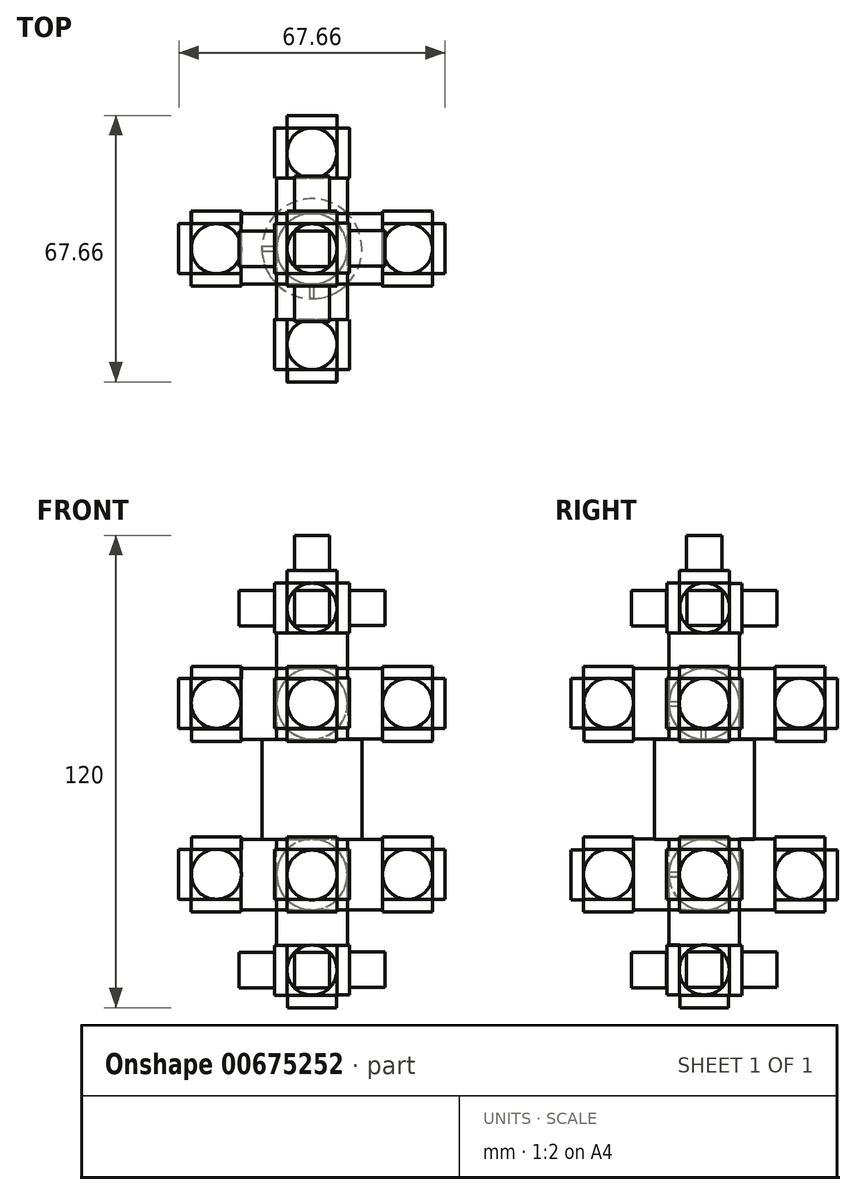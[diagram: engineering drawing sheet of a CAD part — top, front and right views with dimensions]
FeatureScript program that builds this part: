
annotation { "Feature Type Name" : "Feature", "Feature Type Description" : "" }
export const myFeature = defineFeature(function(context is Context, id is Id, definition is map)
    precondition{}
    {
        {
            var Q0;
            Q0=qCreatedBy(makeId("Top.planeOp"),FACE);
            var sketch = newSketch(context, id + "F0", { "sketchPlane" : qUnion([Q0])});
            skCircle(sketch, "E0", {"center": v(0, 0) * mm, "radius": 12.7 * mm});
            skSolve(sketch);
        }
        {
            var Q0;
            Q0=makeQuery(id+"F0.imprint","IMPRINT",FACE,{"disambiguationData":[TD([[makeQuery(id+"F0.imprint","IMPRINT",EDGE,{"derivedFrom":sQuery(id+"F0.wireOp",EDGE,"E0")}),1.0]])]});
            extrude(context, id + "F1", {"entities" : qUnion([Q0]), "depth" : 25.4 * mm, "offsetDistance" : 25.4 * mm});
        }
        {
            var Q0;
            Q0=qCreatedBy(makeId("Top.planeOp"),FACE);
            cPlane(context, id + "F2", {"entities" : qUnion([Q0]), "cplaneType" : CPlaneType.OFFSET, "offset" : 25.4 * mm, "width" : 152.4 * mm, "height" : 152.4 * mm});
        }
        {
            var Q0;
            Q0=qCreatedBy(id+"F2.planeOp",FACE);
            var sketch = newSketch(context, id + "F3", { "sketchPlane" : qUnion([Q0])});
            skLineSegment(sketch, "E1.bottom", {"start": v(-8.98, 8.98) * mm, "end": v(8.98, 8.98) * mm});
            skLineSegment(sketch, "E1.top", {"start": v(-8.98, -8.98) * mm, "end": v(8.98, -8.98) * mm});
            skLineSegment(sketch, "E1.left", {"start": v(-8.98, 8.98) * mm, "end": v(-8.98, -8.98) * mm});
            skLineSegment(sketch, "E1.right", {"start": v(8.98, 8.98) * mm, "end": v(8.98, -8.98) * mm});
            skPoint(sketch, "E1.middle", {"position": v(0, 0) * mm});
            skSolve(sketch);
        }
        {
            var Q0;
            Q0=makeQuery(id+"F3.imprint","IMPRINT",FACE,{"disambiguationData":[TD([[makeQuery(id+"F3.imprint","IMPRINT",EDGE,{"derivedFrom":sQuery(id+"F3.wireOp",EDGE,"E1.bottom")}),-1.0]])]});
            extrude(context, id + "F4", {"entities" : qUnion([Q0]), "operationType" : NewBodyOperationType.ADD, "depth" : 17.96 * mm, "offsetDistance" : 25.4 * mm});
        }
        {
            var Q0;
            Q0=qCreatedBy(makeId("Top.planeOp"),FACE);
            var sketch = newSketch(context, id + "F5", { "sketchPlane" : qUnion([Q0])});
            skLineSegment(sketch, "E2.bottom", {"start": v(-8.98, -8.98) * mm, "end": v(8.98, -8.98) * mm});
            skLineSegment(sketch, "E2.top", {"start": v(-8.98, 8.98) * mm, "end": v(8.98, 8.98) * mm});
            skLineSegment(sketch, "E2.left", {"start": v(-8.98, -8.98) * mm, "end": v(-8.98, 8.98) * mm});
            skLineSegment(sketch, "E2.right", {"start": v(8.98, -8.98) * mm, "end": v(8.98, 8.98) * mm});
            skPoint(sketch, "E2.middle", {"position": v(0, 0) * mm});
            skSolve(sketch);
        }
        {
            var Q0;
            Q0=makeQuery(id+"F5.imprint","IMPRINT",FACE,{"disambiguationData":[TD([[makeQuery(id+"F5.imprint","IMPRINT",EDGE,{"derivedFrom":sQuery(id+"F5.wireOp",EDGE,"E2.bottom")}),1.0]])]});
            extrude(context, id + "F6", {"entities" : qUnion([Q0]), "operationType" : NewBodyOperationType.ADD, "oppositeDirection" : true, "depth" : 17.96 * mm, "offsetDistance" : 25.4 * mm});
        }
        {
            var Q0;
            Q0=qCreatedBy(makeId("Right.planeOp"),FACE);
            cPlane(context, id + "F7", {"entities" : qUnion([Q0]), "cplaneType" : CPlaneType.OFFSET, "offset" : 8.98 * mm, "width" : 152.4 * mm, "height" : 152.4 * mm});
        }
        {
            var Q0;
            Q0=qCreatedBy(makeId("Right.planeOp"),FACE);
            cPlane(context, id + "F8", {"entities" : qUnion([Q0]), "cplaneType" : CPlaneType.OFFSET, "offset" : 8.98 * mm, "oppositeDirection" : true, "width" : 152.4 * mm, "height" : 152.4 * mm});
        }
        {
            var Q0;
            Q0=qCreatedBy(id+"F8.planeOp",FACE);
            var sketch = newSketch(context, id + "F9", { "sketchPlane" : qUnion([Q0])});
            skCircle(sketch, "E3", {"center": v(0, 34.36) * mm, "radius": 8.98 * mm});
            skSolve(sketch);
        }
        {
            var Q0;
            Q0=makeQuery(id+"F9.imprint","IMPRINT",FACE,{"disambiguationData":[TD([[makeQuery(id+"F9.imprint","IMPRINT",EDGE,{"derivedFrom":sQuery(id+"F9.wireOp",EDGE,"E3")}),1.0]])]});
            extrude(context, id + "F10", {"entities" : qUnion([Q0]), "operationType" : NewBodyOperationType.ADD, "oppositeDirection" : true, "depth" : 8.98 * mm, "offsetDistance" : 25.4 * mm});
        }
        {
            var Q0;
            Q0=qCreatedBy(id+"F2.planeOp",FACE);
            cPlane(context, id + "F11", {"entities" : qUnion([Q0]), "cplaneType" : CPlaneType.OFFSET, "offset" : 17.96 * mm, "width" : 152.4 * mm, "height" : 152.4 * mm});
        }
        {
            var Q0;
            Q0=qCreatedBy(id+"F11.planeOp",FACE);
            var sketch = newSketch(context, id + "F12", { "sketchPlane" : qUnion([Q0])});
            skCircle(sketch, "E4", {"center": v(0, 0) * mm, "radius": 8.98 * mm});
            skSolve(sketch);
        }
        {
            var Q0;
            Q0=makeQuery(id+"F12.imprint","IMPRINT",FACE,{"disambiguationData":[TD([[makeQuery(id+"F12.imprint","IMPRINT",EDGE,{"derivedFrom":sQuery(id+"F12.wireOp",EDGE,"E4")}),1.0]])]});
            extrude(context, id + "F13", {"entities" : qUnion([Q0]), "operationType" : NewBodyOperationType.ADD, "depth" : 8.98 * mm, "offsetDistance" : 25.4 * mm});
        }
        {
            var Q0;
            Q0=qCreatedBy(id+"F8.planeOp",FACE);
            var sketch = newSketch(context, id + "F14", { "sketchPlane" : qUnion([Q0])});
            skCircle(sketch, "E5", {"center": v(0, -9.05) * mm, "radius": 8.98 * mm});
            skSolve(sketch);
        }
        {
            var Q0;
            Q0=makeQuery(id+"F14.imprint","IMPRINT",FACE,{"disambiguationData":[TD([[makeQuery(id+"F14.imprint","IMPRINT",EDGE,{"derivedFrom":sQuery(id+"F14.wireOp",EDGE,"E5")}),1.0]])]});
            var Q1;
            Q1=sQuery(id+"F14.wireOp",EDGE,"E5");
            extrude(context, id + "F15", {"entities" : qUnion([Q0]), "operationType" : NewBodyOperationType.ADD, "surfaceEntities" : qUnion([Q1]), "oppositeDirection" : true, "depth" : 8.98 * mm, "offsetDistance" : 25.4 * mm});
        }
        {
            var Q0;
            Q0=qCreatedBy(id+"F7.planeOp",FACE);
            var sketch = newSketch(context, id + "F16", { "sketchPlane" : qUnion([Q0])});
            skCircle(sketch, "E6", {"center": v(0, -9) * mm, "radius": 8.98 * mm});
            skSolve(sketch);
        }
        {
            var Q0;
            Q0=makeQuery(id+"F16.imprint","IMPRINT",FACE,{"disambiguationData":[TD([[makeQuery(id+"F16.imprint","IMPRINT",EDGE,{"derivedFrom":sQuery(id+"F16.wireOp",EDGE,"E6")}),1.0]])]});
            var Q1;
            Q1=sQuery(id+"F16.wireOp",EDGE,"E6");
            extrude(context, id + "F17", {"entities" : qUnion([Q0]), "operationType" : NewBodyOperationType.ADD, "surfaceEntities" : qUnion([Q1]), "depth" : 8.98 * mm, "offsetDistance" : 25.4 * mm});
        }
        {
            var Q0;
            Q0=qCreatedBy(id+"F7.planeOp",FACE);
            var sketch = newSketch(context, id + "F18", { "sketchPlane" : qUnion([Q0])});
            skCircle(sketch, "E7", {"center": v(0, 34.4) * mm, "radius": 8.98 * mm});
            skSolve(sketch);
        }
        {
            var Q0;
            Q0=makeQuery(id+"F18.imprint","IMPRINT",FACE,{"disambiguationData":[TD([[makeQuery(id+"F18.imprint","IMPRINT",EDGE,{"derivedFrom":sQuery(id+"F18.wireOp",EDGE,"E7")}),1.0]])]});
            var Q1;
            Q1=sQuery(id+"F18.wireOp",EDGE,"E7");
            extrude(context, id + "F19", {"entities" : qUnion([Q0]), "operationType" : NewBodyOperationType.ADD, "surfaceEntities" : qUnion([Q1]), "depth" : 8.98 * mm, "offsetDistance" : 25.4 * mm});
        }
        {
            var Q0;
            Q0=qCreatedBy(makeId("Front.planeOp"),FACE);
            cPlane(context, id + "F20", {"entities" : qUnion([Q0]), "cplaneType" : CPlaneType.OFFSET, "offset" : 8.98 * mm, "width" : 152.4 * mm, "height" : 152.4 * mm});
        }
        {
            var Q0;
            Q0=qCreatedBy(id+"F20.planeOp",FACE);
            var sketch = newSketch(context, id + "F21", { "sketchPlane" : qUnion([Q0])});
            skCircle(sketch, "E8", {"center": v(0, -8.96) * mm, "radius": 8.98 * mm});
            skSolve(sketch);
        }
        {
            var Q0;
            Q0=makeQuery(id+"F21.imprint","IMPRINT",FACE,{"disambiguationData":[TD([[makeQuery(id+"F21.imprint","IMPRINT",EDGE,{"derivedFrom":sQuery(id+"F21.wireOp",EDGE,"E8")}),1.0]])]});
            var Q1;
            Q1=sQuery(id+"F21.wireOp",EDGE,"E8");
            extrude(context, id + "F22", {"entities" : qUnion([Q0]), "operationType" : NewBodyOperationType.ADD, "surfaceEntities" : qUnion([Q1]), "depth" : 8.98 * mm, "offsetDistance" : 25.4 * mm});
        }
        {
            var Q0;
            Q0=qCreatedBy(id+"F20.planeOp",FACE);
            var sketch = newSketch(context, id + "F23", { "sketchPlane" : qUnion([Q0])});
            skCircle(sketch, "E9", {"center": v(0, 34.39) * mm, "radius": 8.98 * mm});
            skSolve(sketch);
        }
        {
            var Q0;
            Q0=makeQuery(id+"F23.imprint","IMPRINT",FACE,{"disambiguationData":[TD([[makeQuery(id+"F23.imprint","IMPRINT",EDGE,{"derivedFrom":sQuery(id+"F23.wireOp",EDGE,"E9")}),1.0]])]});
            var Q1;
            Q1=sQuery(id+"F23.wireOp",EDGE,"E9");
            extrude(context, id + "F24", {"entities" : qUnion([Q0]), "surfaceEntities" : qUnion([Q1]), "depth" : 8.98 * mm, "offsetDistance" : 25.4 * mm});
        }
        {
            var Q0;
            Q0=qCreatedBy(makeId("Front.planeOp"),FACE);
            cPlane(context, id + "F25", {"entities" : qUnion([Q0]), "cplaneType" : CPlaneType.OFFSET, "offset" : 8.98 * mm, "oppositeDirection" : true, "width" : 152.4 * mm, "height" : 152.4 * mm});
        }
        {
            var Q0;
            Q0=qCreatedBy(id+"F25.planeOp",FACE);
            var sketch = newSketch(context, id + "F26", { "sketchPlane" : qUnion([Q0])});
            skCircle(sketch, "E10", {"center": v(0, -8.98) * mm, "radius": 8.98 * mm});
            skCircle(sketch, "E11", {"center": v(0, 34.43) * mm, "radius": 8.97 * mm});
            skSolve(sketch);
        }
        {
            var Q0;
            Q0 = qSketchRegion(id + "F26", true);
            extrude(context, id + "F27", {"entities" : qUnion([Q0]), "oppositeDirection" : true, "depth" : 8.98 * mm, "offsetDistance" : 25.4 * mm});
        }
        {
            var Q0;
            Q0=qCreatedBy(makeId("Top.planeOp"),FACE);
            cPlane(context, id + "F28", {"entities" : qUnion([Q0]), "cplaneType" : CPlaneType.OFFSET, "offset" : 17.96 * mm, "oppositeDirection" : true, "width" : 152.4 * mm, "height" : 152.4 * mm});
        }
        {
            var Q0;
            Q0=qCreatedBy(id+"F28.planeOp",FACE);
            var sketch = newSketch(context, id + "F29", { "sketchPlane" : qUnion([Q0])});
            skCircle(sketch, "E12", {"center": v(0, 0) * mm, "radius": 8.98 * mm});
            skSolve(sketch);
        }
        {
            var Q0;
            Q0 = qSketchRegion(id + "F29", true);
            extrude(context, id + "F30", {"entities" : qUnion([Q0]), "oppositeDirection" : true, "depth" : 8.98 * mm, "offsetDistance" : 25.4 * mm});
        }
        {
            var Q0;
            Q0=qCreatedBy(id+"F28.planeOp",FACE);
            cPlane(context, id + "F31", {"entities" : qUnion([Q0]), "cplaneType" : CPlaneType.OFFSET, "offset" : 8.98 * mm, "oppositeDirection" : true, "width" : 152.4 * mm, "height" : 152.4 * mm});
        }
        {
            var Q0;
            Q0=qCreatedBy(id+"F31.planeOp",FACE);
            var sketch = newSketch(context, id + "F32", { "sketchPlane" : qUnion([Q0])});
            skLineSegment(sketch, "E13.bottom", {"start": v(-6.35, -6.35) * mm, "end": v(6.35, -6.35) * mm});
            skLineSegment(sketch, "E13.top", {"start": v(-6.35, 6.35) * mm, "end": v(6.35, 6.35) * mm});
            skLineSegment(sketch, "E13.left", {"start": v(-6.35, -6.35) * mm, "end": v(-6.35, 6.35) * mm});
            skLineSegment(sketch, "E13.right", {"start": v(6.35, -6.35) * mm, "end": v(6.35, 6.35) * mm});
            skPoint(sketch, "E13.middle", {"position": v(0, 0) * mm});
            skSolve(sketch);
        }
        {
            var Q0;
            Q0=makeQuery(id+"F32.imprint","IMPRINT",FACE,{"disambiguationData":[TD([[makeQuery(id+"F32.imprint","IMPRINT",EDGE,{"derivedFrom":sQuery(id+"F32.wireOp",EDGE,"E13.bottom")}),1.0]])]});
            extrude(context, id + "F33", {"entities" : qUnion([Q0]), "operationType" : NewBodyOperationType.ADD, "oppositeDirection" : true, "depth" : 12.7 * mm, "offsetDistance" : 25.4 * mm});
        }
        {
            var Q0;
            Q0=qCreatedBy(id+"F7.planeOp",FACE);
            cPlane(context, id + "F34", {"entities" : qUnion([Q0]), "cplaneType" : CPlaneType.OFFSET, "offset" : 8.98 * mm, "width" : 152.4 * mm, "height" : 152.4 * mm});
        }
        {
            var Q0;
            Q0=qCreatedBy(id+"F34.planeOp",FACE);
            var sketch = newSketch(context, id + "F35", { "sketchPlane" : qUnion([Q0])});
            skLineSegment(sketch, "E14.bottom", {"start": v(-6.35, 40.78) * mm, "end": v(6.35, 40.78) * mm});
            skLineSegment(sketch, "E14.top", {"start": v(-6.35, 28.08) * mm, "end": v(6.35, 28.08) * mm});
            skLineSegment(sketch, "E14.left", {"start": v(-6.35, 40.78) * mm, "end": v(-6.35, 28.08) * mm});
            skLineSegment(sketch, "E14.right", {"start": v(6.35, 40.78) * mm, "end": v(6.35, 28.08) * mm});
            skPoint(sketch, "E14.middle", {"position": v(0, 34.43) * mm});
            skLineSegment(sketch, "E15.bottom", {"start": v(-6.35, -2.63) * mm, "end": v(6.35, -2.63) * mm});
            skLineSegment(sketch, "E15.top", {"start": v(-6.35, -15.33) * mm, "end": v(6.35, -15.33) * mm});
            skLineSegment(sketch, "E15.left", {"start": v(-6.35, -2.63) * mm, "end": v(-6.35, -15.33) * mm});
            skLineSegment(sketch, "E15.right", {"start": v(6.35, -2.63) * mm, "end": v(6.35, -15.33) * mm});
            skPoint(sketch, "E15.middle", {"position": v(0, -8.98) * mm});
            skSolve(sketch);
        }
        {
            var Q0;
            Q0 = qSketchRegion(id + "F35", true);
            extrude(context, id + "F36", {"entities" : qUnion([Q0]), "operationType" : NewBodyOperationType.ADD, "depth" : 12.7 * mm, "offsetDistance" : 25.4 * mm});
        }
        {
            var Q0;
            Q0=qCreatedBy(id+"F8.planeOp",FACE);
            cPlane(context, id + "F37", {"entities" : qUnion([Q0]), "cplaneType" : CPlaneType.OFFSET, "offset" : 8.98 * mm, "oppositeDirection" : true, "width" : 152.4 * mm, "height" : 152.4 * mm});
        }
        {
            var Q0;
            Q0=qCreatedBy(id+"F37.planeOp",FACE);
            var sketch = newSketch(context, id + "F38", { "sketchPlane" : qUnion([Q0])});
            skLineSegment(sketch, "E16.bottom", {"start": v(6.35, -2.63) * mm, "end": v(-6.35, -2.63) * mm});
            skLineSegment(sketch, "E16.top", {"start": v(6.35, -15.33) * mm, "end": v(-6.35, -15.33) * mm});
            skLineSegment(sketch, "E16.left", {"start": v(6.35, -2.63) * mm, "end": v(6.35, -15.33) * mm});
            skLineSegment(sketch, "E16.right", {"start": v(-6.35, -2.63) * mm, "end": v(-6.35, -15.33) * mm});
            skPoint(sketch, "E16.middle", {"position": v(0, -8.98) * mm});
            skLineSegment(sketch, "E17.bottom", {"start": v(6.35, 40.84) * mm, "end": v(-6.35, 40.84) * mm});
            skLineSegment(sketch, "E17.top", {"start": v(6.35, 28.14) * mm, "end": v(-6.35, 28.14) * mm});
            skLineSegment(sketch, "E17.left", {"start": v(6.35, 40.84) * mm, "end": v(6.35, 28.14) * mm});
            skLineSegment(sketch, "E17.right", {"start": v(-6.35, 40.84) * mm, "end": v(-6.35, 28.14) * mm});
            skPoint(sketch, "E17.middle", {"position": v(0, 34.49) * mm});
            skSolve(sketch);
        }
        {
            var Q0;
            Q0 = qSketchRegion(id + "F38", true);
            extrude(context, id + "F39", {"entities" : qUnion([Q0]), "operationType" : NewBodyOperationType.ADD, "oppositeDirection" : true, "depth" : 12.7 * mm, "offsetDistance" : 25.4 * mm});
        }
        {
            var Q0;
            Q0=qCreatedBy(id+"F11.planeOp",FACE);
            cPlane(context, id + "F40", {"entities" : qUnion([Q0]), "cplaneType" : CPlaneType.OFFSET, "offset" : 8.98 * mm, "width" : 152.4 * mm, "height" : 152.4 * mm});
        }
        {
            var Q0;
            Q0=qCreatedBy(id+"F40.planeOp",FACE);
            var sketch = newSketch(context, id + "F41", { "sketchPlane" : qUnion([Q0])});
            skLineSegment(sketch, "E18.bottom", {"start": v(-6.35, 6.35) * mm, "end": v(6.35, 6.35) * mm});
            skLineSegment(sketch, "E18.top", {"start": v(-6.35, -6.35) * mm, "end": v(6.35, -6.35) * mm});
            skLineSegment(sketch, "E18.left", {"start": v(-6.35, 6.35) * mm, "end": v(-6.35, -6.35) * mm});
            skLineSegment(sketch, "E18.right", {"start": v(6.35, 6.35) * mm, "end": v(6.35, -6.35) * mm});
            skPoint(sketch, "E18.middle", {"position": v(0, 0) * mm});
            skSolve(sketch);
        }
        {
            var Q0;
            Q0 = qSketchRegion(id + "F41", true);
            extrude(context, id + "F42", {"entities" : qUnion([Q0]), "depth" : 12.7 * mm, "offsetDistance" : 25.4 * mm});
        }
        {
            var Q0;
            Q0=qCreatedBy(id+"F20.planeOp",FACE);
            cPlane(context, id + "F43", {"entities" : qUnion([Q0]), "cplaneType" : CPlaneType.OFFSET, "offset" : 8.98 * mm, "width" : 152.4 * mm, "height" : 152.4 * mm});
        }
        {
            var Q0;
            Q0=qCreatedBy(id+"F43.planeOp",FACE);
            var sketch = newSketch(context, id + "F44", { "sketchPlane" : qUnion([Q0])});
            skLineSegment(sketch, "E19.bottom", {"start": v(-6.35, -2.63) * mm, "end": v(6.35, -2.63) * mm});
            skLineSegment(sketch, "E19.top", {"start": v(-6.35, -15.33) * mm, "end": v(6.35, -15.33) * mm});
            skLineSegment(sketch, "E19.left", {"start": v(-6.35, -2.63) * mm, "end": v(-6.35, -15.33) * mm});
            skLineSegment(sketch, "E19.right", {"start": v(6.35, -2.63) * mm, "end": v(6.35, -15.33) * mm});
            skPoint(sketch, "E19.middle", {"position": v(0, -8.98) * mm});
            skLineSegment(sketch, "E20.bottom", {"start": v(-6.35, 40.88) * mm, "end": v(6.35, 40.88) * mm});
            skLineSegment(sketch, "E20.top", {"start": v(-6.35, 28.18) * mm, "end": v(6.35, 28.18) * mm});
            skLineSegment(sketch, "E20.left", {"start": v(-6.35, 40.88) * mm, "end": v(-6.35, 28.18) * mm});
            skLineSegment(sketch, "E20.right", {"start": v(6.35, 40.88) * mm, "end": v(6.35, 28.18) * mm});
            skPoint(sketch, "E20.middle", {"position": v(0, 34.53) * mm});
            skSolve(sketch);
        }
        {
            var Q0;
            Q0 = qSketchRegion(id + "F44", true);
            extrude(context, id + "F45", {"entities" : qUnion([Q0]), "depth" : 12.7 * mm, "offsetDistance" : 25.4 * mm});
        }
        {
            var Q0;
            Q0=qCreatedBy(id+"F25.planeOp",FACE);
            cPlane(context, id + "F46", {"entities" : qUnion([Q0]), "cplaneType" : CPlaneType.OFFSET, "offset" : 8.98 * mm, "oppositeDirection" : true, "width" : 152.4 * mm, "height" : 152.4 * mm});
        }
        {
            var Q0;
            Q0=qCreatedBy(id+"F46.planeOp",FACE);
            var sketch = newSketch(context, id + "F47", { "sketchPlane" : qUnion([Q0])});
            skLineSegment(sketch, "E21.bottom", {"start": v(6.35, -2.7) * mm, "end": v(-6.35, -2.7) * mm});
            skLineSegment(sketch, "E21.top", {"start": v(6.35, -15.4) * mm, "end": v(-6.35, -15.4) * mm});
            skLineSegment(sketch, "E21.left", {"start": v(6.35, -2.7) * mm, "end": v(6.35, -15.4) * mm});
            skLineSegment(sketch, "E21.right", {"start": v(-6.35, -2.7) * mm, "end": v(-6.35, -15.4) * mm});
            skPoint(sketch, "E21.middle", {"position": v(0, -9.05) * mm});
            skLineSegment(sketch, "E22.bottom", {"start": v(6.35, 40.87) * mm, "end": v(-6.35, 40.87) * mm});
            skLineSegment(sketch, "E22.top", {"start": v(6.35, 28.17) * mm, "end": v(-6.35, 28.17) * mm});
            skLineSegment(sketch, "E22.left", {"start": v(6.35, 40.87) * mm, "end": v(6.35, 28.17) * mm});
            skLineSegment(sketch, "E22.right", {"start": v(-6.35, 40.87) * mm, "end": v(-6.35, 28.17) * mm});
            skPoint(sketch, "E22.middle", {"position": v(0, 34.52) * mm});
            skSolve(sketch);
        }
        {
            var Q0;
            Q0 = qSketchRegion(id + "F47", true);
            extrude(context, id + "F48", {"entities" : qUnion([Q0]), "oppositeDirection" : true, "depth" : 12.7 * mm, "offsetDistance" : 25.4 * mm});
        }
        {
            var Q0;
            Q0=qCreatedBy(id+"F34.planeOp",FACE);
            cPlane(context, id + "F49", {"entities" : qUnion([Q0]), "cplaneType" : CPlaneType.OFFSET, "offset" : 12.7 * mm, "width" : 152.4 * mm, "height" : 152.4 * mm});
        }
        {
            var Q0;
            Q0=qCreatedBy(id+"F49.planeOp",FACE);
            var sketch = newSketch(context, id + "F50", { "sketchPlane" : qUnion([Q0])});
            skCircle(sketch, "E23", {"center": v(0, -9) * mm, "radius": 6.35 * mm});
            skCircle(sketch, "E24", {"center": v(0, 34.49) * mm, "radius": 6.35 * mm});
            skSolve(sketch);
        }
        {
            var Q0;
            Q0 = qSketchRegion(id + "F50", true);
            extrude(context, id + "F51", {"entities" : qUnion([Q0]), "operationType" : NewBodyOperationType.ADD, "depth" : 3.17 * mm, "offsetDistance" : 25.4 * mm});
        }
        {
            var Q0;
            Q0=qCreatedBy(id+"F37.planeOp",FACE);
            cPlane(context, id + "F52", {"entities" : qUnion([Q0]), "cplaneType" : CPlaneType.OFFSET, "offset" : 12.7 * mm, "oppositeDirection" : true, "width" : 152.4 * mm, "height" : 152.4 * mm});
        }
        {
            var Q0;
            Q0=qCreatedBy(id+"F52.planeOp",FACE);
            var sketch = newSketch(context, id + "F53", { "sketchPlane" : qUnion([Q0])});
            skCircle(sketch, "E25", {"center": v(0, -8.98) * mm, "radius": 6.35 * mm});
            skCircle(sketch, "E26", {"center": v(0, 34.54) * mm, "radius": 6.35 * mm});
            skSolve(sketch);
        }
        {
            var Q0;
            Q0 = qSketchRegion(id + "F53", true);
            extrude(context, id + "F54", {"entities" : qUnion([Q0]), "operationType" : NewBodyOperationType.ADD, "oppositeDirection" : true, "depth" : 3.17 * mm, "offsetDistance" : 25.4 * mm});
        }
        {
            var Q0;
            Q0=qCreatedBy(makeId("Front.planeOp"),FACE);
            cPlane(context, id + "F55", {"entities" : qUnion([Q0]), "cplaneType" : CPlaneType.OFFSET, "offset" : 6.35 * mm, "oppositeDirection" : true, "width" : 152.4 * mm, "height" : 152.4 * mm});
        }
        {
            var Q0;
            Q0=qCreatedBy(id+"F55.planeOp",FACE);
            var sketch = newSketch(context, id + "F56", { "sketchPlane" : qUnion([Q0])});
            skCircle(sketch, "E27", {"center": v(24.33, 34.47) * mm, "radius": 6.35 * mm});
            skCircle(sketch, "E28", {"center": v(24.3, -8.96) * mm, "radius": 6.35 * mm});
            skCircle(sketch, "E29", {"center": v(-24.3, 34.53) * mm, "radius": 6.35 * mm});
            skCircle(sketch, "E30", {"center": v(-24.31, -8.93) * mm, "radius": 6.35 * mm});
            skSolve(sketch);
        }
        {
            var Q0;
            Q0 = qSketchRegion(id + "F56", true);
            extrude(context, id + "F57", {"entities" : qUnion([Q0]), "oppositeDirection" : true, "depth" : 3.17 * mm, "offsetDistance" : 25.4 * mm});
        }
        {
            var Q0;
            Q0=qCreatedBy(id+"F43.planeOp",FACE);
            cPlane(context, id + "F58", {"entities" : qUnion([Q0]), "cplaneType" : CPlaneType.OFFSET, "offset" : 12.7 * mm, "width" : 152.4 * mm, "height" : 152.4 * mm});
        }
        {
            var Q0;
            Q0=qCreatedBy(id+"F58.planeOp",FACE);
            var sketch = newSketch(context, id + "F59", { "sketchPlane" : qUnion([Q0])});
            skCircle(sketch, "E31", {"center": v(0, -9.11) * mm, "radius": 6.35 * mm});
            skCircle(sketch, "E32", {"center": v(0, 34.53) * mm, "radius": 6.25 * mm});
            skSolve(sketch);
        }
        {
            var Q0;
            Q0 = qSketchRegion(id + "F59", true);
            extrude(context, id + "F60", {"entities" : qUnion([Q0]), "depth" : 3.17 * mm, "offsetDistance" : 25.4 * mm});
        }
        {
            var Q0;
            Q0=qCreatedBy(id+"F46.planeOp",FACE);
            cPlane(context, id + "F61", {"entities" : qUnion([Q0]), "cplaneType" : CPlaneType.OFFSET, "offset" : 12.7 * mm, "oppositeDirection" : true, "width" : 152.4 * mm, "height" : 152.4 * mm});
        }
        {
            var Q0;
            Q0=qCreatedBy(id+"F61.planeOp",FACE);
            var sketch = newSketch(context, id + "F62", { "sketchPlane" : qUnion([Q0])});
            skCircle(sketch, "E33", {"center": v(0, 34.5) * mm, "radius": 6.35 * mm});
            skCircle(sketch, "E34", {"center": v(0.04, -9.02) * mm, "radius": 6.35 * mm});
            skSolve(sketch);
        }
        {
            var Q0;
            Q0 = qSketchRegion(id + "F62", true);
            extrude(context, id + "F63", {"entities" : qUnion([Q0]), "oppositeDirection" : true, "depth" : 3.17 * mm, "offsetDistance" : 25.4 * mm});
        }
        {
            var Q0;
            Q0=qCreatedBy(makeId("Front.planeOp"),FACE);
            cPlane(context, id + "F64", {"entities" : qUnion([Q0]), "cplaneType" : CPlaneType.OFFSET, "offset" : 6.38 * mm, "width" : 152.4 * mm, "height" : 152.4 * mm});
        }
        {
            var Q0;
            Q0=qCreatedBy(id+"F64.planeOp",FACE);
            var sketch = newSketch(context, id + "F65", { "sketchPlane" : qUnion([Q0])});
            skCircle(sketch, "E35", {"center": v(-24.32, 34.53) * mm, "radius": 6.35 * mm});
            skCircle(sketch, "E36", {"center": v(24.28, 34.44) * mm, "radius": 6.35 * mm});
            skCircle(sketch, "E37", {"center": v(24.27, -8.94) * mm, "radius": 6.35 * mm});
            skCircle(sketch, "E38", {"center": v(-24.28, -8.92) * mm, "radius": 6.35 * mm});
            skSolve(sketch);
        }
        {
            var Q0;
            Q0 = qSketchRegion(id + "F65", true);
            extrude(context, id + "F66", {"entities" : qUnion([Q0]), "operationType" : NewBodyOperationType.ADD, "depth" : 3.17 * mm, "offsetDistance" : 25.4 * mm});
        }
        {
            var Q0;
            Q0=qCreatedBy(id+"F31.planeOp",FACE);
            cPlane(context, id + "F67", {"entities" : qUnion([Q0]), "cplaneType" : CPlaneType.OFFSET, "offset" : 12.7 * mm, "oppositeDirection" : true, "width" : 152.4 * mm, "height" : 152.4 * mm});
        }
        {
            var Q0;
            Q0=qCreatedBy(id+"F67.planeOp",FACE);
            var sketch = newSketch(context, id + "F68", { "sketchPlane" : qUnion([Q0])});
            skCircle(sketch, "E39", {"center": v(0, 0) * mm, "radius": 6.2 * mm});
            skSolve(sketch);
        }
        {
            var Q0;
            Q0 = qSketchRegion(id + "F68", true);
            extrude(context, id + "F69", {"entities" : qUnion([Q0]), "operationType" : NewBodyOperationType.ADD, "oppositeDirection" : true, "depth" : 3.17 * mm, "offsetDistance" : 25.4 * mm});
        }
        {
            var Q0;
            Q0=qCreatedBy(id+"F40.planeOp",FACE);
            cPlane(context, id + "F70", {"entities" : qUnion([Q0]), "cplaneType" : CPlaneType.OFFSET, "offset" : 12.7 * mm, "width" : 152.4 * mm, "height" : 152.4 * mm});
        }
        {
            var Q0;
            Q0=qCreatedBy(id+"F70.planeOp",FACE);
            var sketch = newSketch(context, id + "F71", { "sketchPlane" : qUnion([Q0])});
            skCircle(sketch, "E40", {"center": v(0, 0) * mm, "radius": 6.34 * mm});
            skSolve(sketch);
        }
        {
            var Q0;
            Q0 = qSketchRegion(id + "F71", true);
            extrude(context, id + "F72", {"entities" : qUnion([Q0]), "operationType" : NewBodyOperationType.ADD, "depth" : 3.17 * mm, "offsetDistance" : 25.4 * mm});
        }
        {
            var Q0;
            Q0=qCreatedBy(makeId("Right.planeOp"),FACE);
            cPlane(context, id + "F73", {"entities" : qUnion([Q0]), "cplaneType" : CPlaneType.OFFSET, "offset" : 6.35 * mm, "width" : 152.4 * mm, "height" : 152.4 * mm});
        }
        {
            var Q0;
            Q0=qCreatedBy(id+"F73.planeOp",FACE);
            var sketch = newSketch(context, id + "F74", { "sketchPlane" : qUnion([Q0])});
            skCircle(sketch, "E41", {"center": v(-24.3, 34.57) * mm, "radius": 6.35 * mm});
            skCircle(sketch, "E42", {"center": v(24.3, 34.56) * mm, "radius": 6.35 * mm});
            skCircle(sketch, "E43", {"center": v(24.32, -9.03) * mm, "radius": 6.35 * mm});
            skCircle(sketch, "E44", {"center": v(-24.3, -8.94) * mm, "radius": 6.35 * mm});
            skSolve(sketch);
        }
        {
            var Q0;
            Q0 = qSketchRegion(id + "F74", true);
            extrude(context, id + "F75", {"entities" : qUnion([Q0]), "depth" : 3.17 * mm, "offsetDistance" : 25.4 * mm});
        }
        {
            var Q0;
            Q0=qCreatedBy(makeId("Right.planeOp"),FACE);
            cPlane(context, id + "F76", {"entities" : qUnion([Q0]), "cplaneType" : CPlaneType.OFFSET, "offset" : 6.35 * mm, "oppositeDirection" : true, "width" : 152.4 * mm, "height" : 152.4 * mm});
        }
        {
            var Q0;
            Q0=qCreatedBy(id+"F76.planeOp",FACE);
            var sketch = newSketch(context, id + "F77", { "sketchPlane" : qUnion([Q0])});
            skCircle(sketch, "E45", {"center": v(24.3, 34.53) * mm, "radius": 6.35 * mm});
            skCircle(sketch, "E46", {"center": v(-24.31, 34.54) * mm, "radius": 6.35 * mm});
            skCircle(sketch, "E47", {"center": v(-24.3, -8.97) * mm, "radius": 6.35 * mm});
            skCircle(sketch, "E48", {"center": v(24.32, -9.02) * mm, "radius": 6.35 * mm});
            skSolve(sketch);
        }
        {
            var Q0;
            Q0 = qSketchRegion(id + "F77", true);
            extrude(context, id + "F78", {"entities" : qUnion([Q0]), "oppositeDirection" : true, "depth" : 3.17 * mm, "offsetDistance" : 25.4 * mm});
        }
        {
            var Q0;
            Q0=qCreatedBy(id+"F11.planeOp",FACE);
            cPlane(context, id + "F79", {"entities" : qUnion([Q0]), "cplaneType" : CPlaneType.OFFSET, "offset" : 2.63 * mm, "oppositeDirection" : true, "width" : 152.4 * mm, "height" : 152.4 * mm});
        }
        {
            var Q0;
            Q0=qCreatedBy(id+"F79.planeOp",FACE);
            var sketch = newSketch(context, id + "F80", { "sketchPlane" : qUnion([Q0])});
            skCircle(sketch, "E49", {"center": v(-0.02, 24.3) * mm, "radius": 6.35 * mm});
            skCircle(sketch, "E50", {"center": v(0.03, -24.36) * mm, "radius": 6.35 * mm});
            skCircle(sketch, "E51", {"center": v(24.3, 0) * mm, "radius": 6.35 * mm});
            skCircle(sketch, "E52", {"center": v(-24.3, 0) * mm, "radius": 6.35 * mm});
            skSolve(sketch);
        }
        {
            var Q0;
            Q0 = qSketchRegion(id + "F80", true);
            extrude(context, id + "F81", {"entities" : qUnion([Q0]), "depth" : 3.17 * mm, "offsetDistance" : 25.4 * mm});
        }
        {
            var Q0;
            Q0=qCreatedBy(id+"F28.planeOp",FACE);
            cPlane(context, id + "F82", {"entities" : qUnion([Q0]), "cplaneType" : CPlaneType.OFFSET, "offset" : 2.63 * mm, "width" : 152.4 * mm, "height" : 152.4 * mm});
        }
        {
            var Q0;
            Q0=qCreatedBy(id+"F82.planeOp",FACE);
            var sketch = newSketch(context, id + "F83", { "sketchPlane" : qUnion([Q0])});
            skCircle(sketch, "E53", {"center": v(0, 24.28) * mm, "radius": 6.35 * mm});
            skCircle(sketch, "E54", {"center": v(24.32, 0) * mm, "radius": 6.35 * mm});
            skCircle(sketch, "E55", {"center": v(0, -24.37) * mm, "radius": 6.35 * mm});
            skCircle(sketch, "E56", {"center": v(-24.36, 0) * mm, "radius": 6.35 * mm});
            skSolve(sketch);
        }
        {
            var Q0;
            Q0 = qSketchRegion(id + "F83", true);
            extrude(context, id + "F84", {"entities" : qUnion([Q0]), "oppositeDirection" : true, "depth" : 3.17 * mm, "offsetDistance" : 25.4 * mm});
        }
        {
            var Q0;
            Q0=qCreatedBy(makeId("Right.planeOp"),FACE);
            cPlane(context, id + "F85", {"entities" : qUnion([Q0]), "cplaneType" : CPlaneType.OFFSET, "offset" : 6.35 * mm, "width" : 152.4 * mm, "height" : 152.4 * mm});
        }
        {
            var Q0;
            Q0=qCreatedBy(id+"F85.planeOp",FACE);
            var sketch = newSketch(context, id + "F86", { "sketchPlane" : qUnion([Q0])});
            skCircle(sketch, "E57", {"center": v(0.12, 58.74) * mm, "radius": 6.35 * mm});
            skCircle(sketch, "E58", {"center": v(0, -33.22) * mm, "radius": 6.35 * mm});
            skSolve(sketch);
        }
        {
            var Q0;
            Q0 = qSketchRegion(id + "F86", true);
            extrude(context, id + "F87", {"entities" : qUnion([Q0]), "depth" : 3.17 * mm, "offsetDistance" : 25.4 * mm});
        }
        {
            var Q0;
            Q0=qCreatedBy(makeId("Front.planeOp"),FACE);
            cPlane(context, id + "F88", {"entities" : qUnion([Q0]), "cplaneType" : CPlaneType.OFFSET, "offset" : 6.35 * mm, "width" : 152.4 * mm, "height" : 152.4 * mm});
        }
        {
            var Q0;
            Q0=qCreatedBy(id+"F88.planeOp",FACE);
            var sketch = newSketch(context, id + "F89", { "sketchPlane" : qUnion([Q0])});
            skCircle(sketch, "E59", {"center": v(0, 58.69) * mm, "radius": 6.35 * mm});
            skCircle(sketch, "E60", {"center": v(0, -33.26) * mm, "radius": 6.35 * mm});
            skSolve(sketch);
        }
        {
            var Q0;
            Q0 = qSketchRegion(id + "F89", true);
            extrude(context, id + "F90", {"entities" : qUnion([Q0]), "depth" : 3.17 * mm, "offsetDistance" : 25.4 * mm});
        }
        {
            var Q0;
            Q0=qCreatedBy(makeId("Right.planeOp"),FACE);
            cPlane(context, id + "F91", {"entities" : qUnion([Q0]), "cplaneType" : CPlaneType.OFFSET, "offset" : 6.35 * mm, "oppositeDirection" : true, "width" : 152.4 * mm, "height" : 152.4 * mm});
        }
        {
            var Q0;
            Q0=qCreatedBy(id+"F91.planeOp",FACE);
            var sketch = newSketch(context, id + "F92", { "sketchPlane" : qUnion([Q0])});
            skCircle(sketch, "E61", {"center": v(0, 58.7) * mm, "radius": 6.35 * mm});
            skCircle(sketch, "E62", {"center": v(0, -33.27) * mm, "radius": 6.35 * mm});
            skSolve(sketch);
        }
        {
            var Q0;
            Q0 = qSketchRegion(id + "F92", true);
            extrude(context, id + "F93", {"entities" : qUnion([Q0]), "oppositeDirection" : true, "depth" : 3.17 * mm, "offsetDistance" : 25.4 * mm});
        }
        {
            var Q0;
            Q0=qCreatedBy(makeId("Front.planeOp"),FACE);
            cPlane(context, id + "F94", {"entities" : qUnion([Q0]), "cplaneType" : CPlaneType.OFFSET, "offset" : 6.35 * mm, "oppositeDirection" : true, "width" : 152.4 * mm, "height" : 152.4 * mm});
        }
        {
            var Q0;
            Q0=qCreatedBy(id+"F94.planeOp",FACE);
            var sketch = newSketch(context, id + "F95", { "sketchPlane" : qUnion([Q0])});
            skCircle(sketch, "E63", {"center": v(-0.03, 58.67) * mm, "radius": 6.35 * mm});
            skCircle(sketch, "E64", {"center": v(0, -33.3) * mm, "radius": 6.35 * mm});
            skSolve(sketch);
        }
        {
            var Q0;
            Q0 = qSketchRegion(id + "F95", true);
            extrude(context, id + "F96", {"entities" : qUnion([Q0]), "oppositeDirection" : true, "depth" : 3.17 * mm, "offsetDistance" : 25.4 * mm});
        }
        {
            var Q0;
            Q0=qCreatedBy(makeId("Top.planeOp"),FACE);
            cPlane(context, id + "F97", {"entities" : qUnion([Q0]), "cplaneType" : CPlaneType.OFFSET, "offset" : 2.63 * mm, "oppositeDirection" : true, "width" : 152.4 * mm, "height" : 152.4 * mm});
        }
        {
            var Q0;
            Q0=qCreatedBy(id+"F97.planeOp",FACE);
            var sketch = newSketch(context, id + "F98", { "sketchPlane" : qUnion([Q0])});
            skCircle(sketch, "E65", {"center": v(0, 24.37) * mm, "radius": 6.35 * mm});
            skCircle(sketch, "E66", {"center": v(-24.26, 0) * mm, "radius": 6.35 * mm});
            skCircle(sketch, "E67", {"center": v(24.3, 0) * mm, "radius": 6.33 * mm});
            skCircle(sketch, "E68", {"center": v(0, -24.31) * mm, "radius": 6.35 * mm});
            skSolve(sketch);
        }
        {
            var Q0;
            Q0 = qSketchRegion(id + "F98", true);
            extrude(context, id + "F99", {"entities" : qUnion([Q0]), "depth" : 3.17 * mm, "offsetDistance" : 25.4 * mm});
        }
        {
            var Q0;
            Q0=qCreatedBy(id+"F2.planeOp",FACE);
            cPlane(context, id + "F100", {"entities" : qUnion([Q0]), "cplaneType" : CPlaneType.OFFSET, "offset" : 2.63 * mm, "width" : 152.4 * mm, "height" : 152.4 * mm});
        }
        {
            var Q0;
            Q0=qCreatedBy(id+"F100.planeOp",FACE);
            var sketch = newSketch(context, id + "F101", { "sketchPlane" : qUnion([Q0])});
            skCircle(sketch, "E69", {"center": v(0, 24.46) * mm, "radius": 6.36 * mm});
            skCircle(sketch, "E70", {"center": v(24.3, 0) * mm, "radius": 6.35 * mm});
            skCircle(sketch, "E71", {"center": v(-24.28, -0.15) * mm, "radius": 6.35 * mm});
            skCircle(sketch, "E72", {"center": v(0, -24.32) * mm, "radius": 6.29 * mm});
            skSolve(sketch);
        }
        {
            var Q0;
            Q0 = qSketchRegion(id + "F101", true);
            extrude(context, id + "F102", {"entities" : qUnion([Q0]), "operationType" : NewBodyOperationType.ADD, "oppositeDirection" : true, "depth" : 3.17 * mm, "offsetDistance" : 25.4 * mm});
        }
        {
            var Q0;
            Q0=qCreatedBy(id+"F70.planeOp",FACE);
            cPlane(context, id + "F103", {"entities" : qUnion([Q0]), "cplaneType" : CPlaneType.OFFSET, "offset" : 3.17 * mm, "width" : 152.4 * mm, "height" : 152.4 * mm});
        }
        {
            var Q0;
            Q0=qCreatedBy(id+"F103.planeOp",FACE);
            var sketch = newSketch(context, id + "F104", { "sketchPlane" : qUnion([Q0])});
            skLineSegment(sketch, "E73.bottom", {"start": v(-4.5, 4.5) * mm, "end": v(4.5, 4.5) * mm});
            skLineSegment(sketch, "E73.top", {"start": v(-4.5, -4.5) * mm, "end": v(4.5, -4.5) * mm});
            skLineSegment(sketch, "E73.left", {"start": v(-4.5, 4.5) * mm, "end": v(-4.5, -4.5) * mm});
            skLineSegment(sketch, "E73.right", {"start": v(4.5, 4.5) * mm, "end": v(4.5, -4.5) * mm});
            skPoint(sketch, "E73.middle", {"position": v(0, 0) * mm});
            skSolve(sketch);
        }
        {
            var Q0;
            Q0=qCreatedBy(id+"F85.planeOp",FACE);
            cPlane(context, id + "F105", {"entities" : qUnion([Q0]), "cplaneType" : CPlaneType.OFFSET, "offset" : 3.17 * mm, "width" : 152.4 * mm, "height" : 152.4 * mm});
        }
        {
            var Q0;
            Q0=qCreatedBy(id+"F105.planeOp",FACE);
            var sketch = newSketch(context, id + "F106", { "sketchPlane" : qUnion([Q0])});
            skLineSegment(sketch, "E74.bottom", {"start": v(-4.4, 63.22) * mm, "end": v(4.59, 63.22) * mm});
            skLineSegment(sketch, "E74.top", {"start": v(-4.4, 54.24) * mm, "end": v(4.59, 54.24) * mm});
            skLineSegment(sketch, "E74.left", {"start": v(-4.4, 63.22) * mm, "end": v(-4.4, 54.24) * mm});
            skLineSegment(sketch, "E74.right", {"start": v(4.59, 63.22) * mm, "end": v(4.59, 54.24) * mm});
            skPoint(sketch, "E74.middle", {"position": v(0.1, 58.73) * mm});
            skLineSegment(sketch, "E75.bottom", {"start": v(-4.5, -28.67) * mm, "end": v(4.5, -28.67) * mm});
            skLineSegment(sketch, "E75.top", {"start": v(-4.5, -37.65) * mm, "end": v(4.5, -37.65) * mm});
            skLineSegment(sketch, "E75.left", {"start": v(-4.5, -28.67) * mm, "end": v(-4.5, -37.65) * mm});
            skLineSegment(sketch, "E75.right", {"start": v(4.5, -28.67) * mm, "end": v(4.5, -37.65) * mm});
            skPoint(sketch, "E75.middle", {"position": v(0, -33.16) * mm});
            skSolve(sketch);
        }
        {
            var Q0;
            Q0 = qSketchRegion(id + "F104", true);
            extrude(context, id + "F107", {"entities" : qUnion([Q0]), "operationType" : NewBodyOperationType.ADD, "depth" : 8.98 * mm, "offsetDistance" : 25.4 * mm});
        }
        {
            var Q0;
            Q0 = qSketchRegion(id + "F106", true);
            extrude(context, id + "F108", {"entities" : qUnion([Q0]), "depth" : 8.98 * mm, "offsetDistance" : 25.4 * mm});
        }
        {
            var Q0;
            Q0=qCreatedBy(id+"F64.planeOp",FACE);
            cPlane(context, id + "F109", {"entities" : qUnion([Q0]), "cplaneType" : CPlaneType.OFFSET, "offset" : 3.17 * mm, "width" : 152.4 * mm, "height" : 152.4 * mm});
        }
        {
            var Q0;
            Q0=qCreatedBy(id+"F109.planeOp",FACE);
            var sketch = newSketch(context, id + "F110", { "sketchPlane" : qUnion([Q0])});
            skLineSegment(sketch, "E76.bottom", {"start": v(-4.5, 63.21) * mm, "end": v(4.5, 63.21) * mm});
            skLineSegment(sketch, "E76.top", {"start": v(-4.5, 54.23) * mm, "end": v(4.5, 54.23) * mm});
            skLineSegment(sketch, "E76.left", {"start": v(-4.5, 63.21) * mm, "end": v(-4.5, 54.23) * mm});
            skLineSegment(sketch, "E76.right", {"start": v(4.5, 63.21) * mm, "end": v(4.5, 54.23) * mm});
            skPoint(sketch, "E76.middle", {"position": v(0, 58.72) * mm});
            skLineSegment(sketch, "E77.bottom", {"start": v(-4.5, -28.76) * mm, "end": v(4.5, -28.76) * mm});
            skLineSegment(sketch, "E77.top", {"start": v(-4.5, -37.74) * mm, "end": v(4.5, -37.74) * mm});
            skLineSegment(sketch, "E77.left", {"start": v(-4.5, -28.76) * mm, "end": v(-4.5, -37.74) * mm});
            skLineSegment(sketch, "E77.right", {"start": v(4.5, -28.76) * mm, "end": v(4.5, -37.74) * mm});
            skPoint(sketch, "E77.middle", {"position": v(0, -33.25) * mm});
            skSolve(sketch);
        }
        {
            var Q0;
            Q0 = qSketchRegion(id + "F110", true);
            extrude(context, id + "F111", {"entities" : qUnion([Q0]), "depth" : 8.98 * mm, "offsetDistance" : 25.4 * mm});
        }
        {
            var Q0;
            Q0=qCreatedBy(id+"F76.planeOp",FACE);
            cPlane(context, id + "F112", {"entities" : qUnion([Q0]), "cplaneType" : CPlaneType.OFFSET, "offset" : 3.17 * mm, "oppositeDirection" : true, "width" : 152.4 * mm, "height" : 152.4 * mm});
        }
        {
            var Q0;
            Q0=qCreatedBy(id+"F112.planeOp",FACE);
            var sketch = newSketch(context, id + "F113", { "sketchPlane" : qUnion([Q0])});
            skLineSegment(sketch, "E78.bottom", {"start": v(4.5, 63.19) * mm, "end": v(-4.5, 63.19) * mm});
            skLineSegment(sketch, "E78.top", {"start": v(4.5, 54.2) * mm, "end": v(-4.5, 54.2) * mm});
            skLineSegment(sketch, "E78.left", {"start": v(4.5, 63.19) * mm, "end": v(4.5, 54.2) * mm});
            skLineSegment(sketch, "E78.right", {"start": v(-4.5, 63.19) * mm, "end": v(-4.5, 54.2) * mm});
            skPoint(sketch, "E78.middle", {"position": v(0, 58.7) * mm});
            skLineSegment(sketch, "E79.bottom", {"start": v(4.5, -28.78) * mm, "end": v(-4.5, -28.78) * mm});
            skLineSegment(sketch, "E79.top", {"start": v(4.5, -37.76) * mm, "end": v(-4.5, -37.76) * mm});
            skLineSegment(sketch, "E79.left", {"start": v(4.5, -28.78) * mm, "end": v(4.5, -37.76) * mm});
            skLineSegment(sketch, "E79.right", {"start": v(-4.5, -28.78) * mm, "end": v(-4.5, -37.76) * mm});
            skPoint(sketch, "E79.middle", {"position": v(0, -33.27) * mm});
            skSolve(sketch);
        }
        {
            var Q0;
            Q0 = qSketchRegion(id + "F113", true);
            extrude(context, id + "F114", {"entities" : qUnion([Q0]), "oppositeDirection" : true, "depth" : 8.98 * mm, "offsetDistance" : 25.4 * mm});
        }
        {
            var Q0;
            Q0=qCreatedBy(id+"F94.planeOp",FACE);
            cPlane(context, id + "F115", {"entities" : qUnion([Q0]), "cplaneType" : CPlaneType.OFFSET, "offset" : 3.17 * mm, "oppositeDirection" : true, "width" : 152.4 * mm, "height" : 152.4 * mm});
        }
        {
            var Q0;
            Q0=qCreatedBy(id+"F115.planeOp",FACE);
            var sketch = newSketch(context, id + "F116", { "sketchPlane" : qUnion([Q0])});
            skLineSegment(sketch, "E80.bottom", {"start": v(4.5, 63.16) * mm, "end": v(-4.5, 63.16) * mm});
            skLineSegment(sketch, "E80.top", {"start": v(4.5, 54.18) * mm, "end": v(-4.5, 54.18) * mm});
            skLineSegment(sketch, "E80.left", {"start": v(4.5, 63.16) * mm, "end": v(4.5, 54.18) * mm});
            skLineSegment(sketch, "E80.right", {"start": v(-4.5, 63.16) * mm, "end": v(-4.5, 54.18) * mm});
            skPoint(sketch, "E80.middle", {"position": v(0, 58.67) * mm});
            skLineSegment(sketch, "E81.bottom", {"start": v(4.5, -28.7) * mm, "end": v(-4.5, -28.7) * mm});
            skLineSegment(sketch, "E81.top", {"start": v(4.5, -37.67) * mm, "end": v(-4.5, -37.67) * mm});
            skLineSegment(sketch, "E81.left", {"start": v(4.5, -28.7) * mm, "end": v(4.5, -37.67) * mm});
            skLineSegment(sketch, "E81.right", {"start": v(-4.5, -28.7) * mm, "end": v(-4.5, -37.67) * mm});
            skPoint(sketch, "E81.middle", {"position": v(0, -33.18) * mm});
            skSolve(sketch);
        }
        {
            var Q0;
            Q0 = qSketchRegion(id + "F116", true);
            extrude(context, id + "F117", {"entities" : qUnion([Q0]), "oppositeDirection" : true, "depth" : 8.98 * mm, "offsetDistance" : 25.4 * mm});
        }
    });
